# Revit family: equip-sink-elkay-lav-wall
name_source: partatom
category: Plumbing Fixtures
units: mm (PartAtom-declared; Revit-internal decimal feet)

## family parameters
Cut with Voids When Loaded = No
Host = Face
Part Type = Normal
Room Calculation Point = No
Round Connector Dimension = Use Radius
Shared = No

## types (10) — shared parameters
Assembly Code = D2010410
Bowl Drain Location FB = 0' - 3 1/2"
Bubbler CW Flow Rate = 2 GPM
Bubbler Material = Metal - Steel - Stainless - Chrome
Bubbler Nominal Dia = 0' - 0 1/2"
Bubbler Nominal Radius = 0' - 0 1/4"
CW Flow Rate = 2 GPM
Cost = -1 $
Default Elevation = 2' - 7 1/2"
Description = Wash-Up Lavatory Sinks
Drain Material = Metal - Steel - Stainless - Chrome
Faucet CL to Wall = 0' - 2 1/2"
Faucet Material = Metal - Steel - Stainless - Chrome
HW Flow Rate = 2 GPM
Keynote = D2010410
Manufacturer = Elkay Manufacturing
MasterFormat Number = 22.42.16.16
MasterFormat Title = Commercial Sinks
Nominal Dia = 0' - 0 1/2"
Nominal Radius = 0' - 0 1/4"
OmniClass Code = 23.45.05.14.14.27
OmniClass Title = Service Sinks
Reference Level to Back Plane = 0' - 0"
Sanitary Flow Rate = 10 GPM
Sanitary Nominal Dia = 0' - 1 1/2"
Sanitary Nominal Radius = 0' - 0 3/4"
Sink Ledge Back Width = 0' - 4 1/2"
Sink Ledge Back Width Hidden = 0' - 4 1/2"
Sink Material = Metal - Steel - Stainless - Chrome
Specification Sheet URL = http://www.elkayusa.com
Stem Material = Metal - Steel
URL = www.elkayusa.com
Vent Connection = Yes
zero-valued in all types: CWFU, HWFU, WFU

## per-type parameters (varying)
- ELVWO22193: Backsplash Height=0' - 2 3/4"; Bowl Depth=0' - 5 1/2"; Bowl Length=1' - 4"; Bowl Width=0' - 11 1/2"; Drain CL LR to Left Bowl Edge=0' - 8"; Faucet Hole Dia=0' - 1 1/2"; Faucet Hole One=Yes; Faucet Hole One Top=0' - 0 1/4"; Faucet Hole One to CL=0' - 4"; Faucet Hole Three=Yes; Faucet Hole Three Top=0' - 0 1/4"; Faucet Hole Two=Yes; Faucet Hole Two Top=0' - 0 1/4"; Hole One to Three=0' - 8"; Hole One to Two=0' - 4"; Hole Radius=0' - 0 3/4"; OverFlow=Yes; Overflow Void=0' - 0 3/16"; Sink Ledge Front Width=0' - 3"; Sink Ledge Front Width Hidden=0' - 3"; Sink Ledge Left Width=0' - 3"; Sink Ledge Left Width Hidden=0' - 3"; Sink Ledge Right Width=0' - 3"; Sink Ledge Right Width Hidden=0' - 3"; Sink Length=1' - 10"; Sink Width=1' - 7"
- ELVWO2219CS3: Backsplash Height=0' - 2 3/4"; Bowl Depth=0' - 5 1/2"; Bowl Length=1' - 4"; Bowl Width=0' - 11 1/2"; Drain CL LR to Left Bowl Edge=0' - 8"; Faucet Hole Dia=0' - 1 1/4"; Faucet Hole One=Yes; Faucet Hole One Top=0' - 0 1/4"; Faucet Hole One to CL=0' - 2"; Faucet Hole Three=Yes; Faucet Hole Three Top=0' - 0 1/4"; Faucet Hole Two=Yes; Faucet Hole Two Top=0' - 0 1/4"; Hole One to Three=0' - 4"; Hole One to Two=0' - 2"; Hole Radius=0' - 0 5/8"; OverFlow=Yes; Overflow Void=0' - 0 3/16"; Sink Ledge Front Width=0' - 3"; Sink Ledge Front Width Hidden=0' - 3"; Sink Ledge Left Width=0' - 3"; Sink Ledge Left Width Hidden=0' - 3"; Sink Ledge Right Width=0' - 3"; Sink Ledge Right Width Hidden=0' - 3"; Sink Length=1' - 10"; Sink Width=1' - 7"
- ELVWO22191: Backsplash Height=0' - 2 3/4"; Bowl Depth=0' - 5 1/2"; Bowl Length=1' - 4"; Bowl Width=0' - 11 1/2"; Drain CL LR to Left Bowl Edge=0' - 8"; Faucet Hole Dia=0' - 1 1/4"; Faucet Hole One=No; Faucet Hole One Top=0' - 0 1/8"; Faucet Hole One to CL=0' - 2"; Faucet Hole Three=No; Faucet Hole Three Top=0' - 0 1/8"; Faucet Hole Two=Yes; Faucet Hole Two Top=0' - 0 1/4"; Hole One to Three=0' - 4"; Hole One to Two=0' - 2"; Hole Radius=0' - 0 5/8"; OverFlow=Yes; Overflow Void=0' - 0 3/16"; Sink Ledge Front Width=0' - 3"; Sink Ledge Front Width Hidden=0' - 3"; Sink Ledge Left Width=0' - 3"; Sink Ledge Left Width Hidden=0' - 3"; Sink Ledge Right Width=0' - 3"; Sink Ledge Right Width Hidden=0' - 3"; Sink Length=1' - 10"; Sink Width=1' - 7"
- WCLWO1923OSD3: Backsplash Height=0' - 2 1/2"; Bowl Depth=0' - 4"; Bowl Length=1' - 1 1/2"; Bowl Width=1' - 4"; Drain CL LR to Left Bowl Edge=0' - 6 3/4"; Faucet Hole Dia=0' - 1 1/4"; Faucet Hole One=Yes; Faucet Hole One Top=0' - 0 1/4"; Faucet Hole One to CL=0' - 4"; Faucet Hole Three=Yes; Faucet Hole Three Top=0' - 0 1/4"; Faucet Hole Two=Yes; Faucet Hole Two Top=0' - 0 1/4"; Hole One to Three=0' - 8"; Hole One to Two=0' - 4"; Hole Radius=0' - 0 5/8"; OverFlow=Yes; Overflow Void=0' - 0 3/16"; Sink Ledge Front Width=0' - 2 1/2"; Sink Ledge Front Width Hidden=0' - 2 1/2"; Sink Ledge Left Width=0' - 2 3/4"; Sink Ledge Left Width Hidden=0' - 2 3/4"; Sink Ledge Right Width=0' - 2 3/4"; Sink Ledge Right Width Hidden=0' - 2 3/4"; Sink Length=1' - 7"; Sink Width=1' - 11"
- ELV22193: Backsplash Height=0' - 2 3/4"; Bowl Depth=0' - 5 1/2"; Bowl Length=1' - 4"; Bowl Width=0' - 11 1/2"; Drain CL LR to Left Bowl Edge=0' - 8"; Faucet Hole Dia=0' - 1 1/2"; Faucet Hole One=Yes; Faucet Hole One Top=0' - 0 1/4"; Faucet Hole One to CL=0' - 4"; Faucet Hole Three=Yes; Faucet Hole Three Top=0' - 0 1/4"; Faucet Hole Two=Yes; Faucet Hole Two Top=0' - 0 1/4"; Hole One to Three=0' - 8"; Hole One to Two=0' - 4"; Hole Radius=0' - 0 3/4"; OverFlow=No; Overflow Void=0' - 0 1/16"; Sink Ledge Front Width=0' - 3"; Sink Ledge Front Width Hidden=0' - 3"; Sink Ledge Left Width=0' - 3"; Sink Ledge Left Width Hidden=0' - 3"; Sink Ledge Right Width=0' - 3"; Sink Ledge Right Width Hidden=0' - 3"; Sink Length=1' - 10"; Sink Width=1' - 7"
- ELV22191: Backsplash Height=0' - 2 3/4"; Bowl Depth=0' - 5 1/2"; Bowl Length=1' - 4"; Bowl Width=0' - 11 1/2"; Drain CL LR to Left Bowl Edge=0' - 8"; Faucet Hole Dia=0' - 1 1/4"; Faucet Hole One=No; Faucet Hole One Top=0' - 0 1/8"; Faucet Hole One to CL=0' - 2"; Faucet Hole Three=No; Faucet Hole Three Top=0' - 0 1/8"; Faucet Hole Two=Yes; Faucet Hole Two Top=0' - 0 1/4"; Hole One to Three=0' - 4"; Hole One to Two=0' - 2"; Hole Radius=0' - 0 5/8"; OverFlow=No; Overflow Void=0' - 0 1/16"; Sink Ledge Front Width=0' - 3"; Sink Ledge Front Width Hidden=0' - 3"; Sink Ledge Left Width=0' - 3"; Sink Ledge Left Width Hidden=0' - 3"; Sink Ledge Right Width=0' - 3"; Sink Ledge Right Width Hidden=0' - 3"; Sink Length=1' - 10"; Sink Width=1' - 7"
- WCL1923OSD1: Backsplash Height=0' - 2 1/2"; Bowl Depth=0' - 4"; Bowl Length=1' - 2"; Bowl Width=1' - 4"; Drain CL LR to Left Bowl Edge=0' - 7"; Faucet Hole Dia=0' - 1 1/4"; Faucet Hole One=No; Faucet Hole One Top=0' - 0 1/8"; Faucet Hole One to CL=0' - 4"; Faucet Hole Three=No; Faucet Hole Three Top=0' - 0 1/8"; Faucet Hole Two=Yes; Faucet Hole Two Top=0' - 0 1/4"; Hole One to Three=0' - 8"; Hole One to Two=0' - 4"; Hole Radius=0' - 0 5/8"; OverFlow=No; Overflow Void=0' - 0 1/16"; Sink Ledge Front Width=0' - 2 1/2"; Sink Ledge Front Width Hidden=0' - 2 1/2"; Sink Ledge Left Width=0' - 2 1/2"; Sink Ledge Left Width Hidden=0' - 2 1/2"; Sink Ledge Right Width=0' - 2 1/2"; Sink Ledge Right Width Hidden=0' - 2 1/2"; Sink Length=1' - 7"; Sink Width=1' - 11"
- ELV2219CS3: Backsplash Height=0' - 2 3/4"; Bowl Depth=0' - 5 1/2"; Bowl Length=1' - 4"; Bowl Width=0' - 11 1/2"; Drain CL LR to Left Bowl Edge=0' - 8"; Faucet Hole Dia=0' - 1 1/4"; Faucet Hole One=Yes; Faucet Hole One Top=0' - 0 1/4"; Faucet Hole One to CL=0' - 2"; Faucet Hole Three=Yes; Faucet Hole Three Top=0' - 0 1/4"; Faucet Hole Two=Yes; Faucet Hole Two Top=0' - 0 1/4"; Hole One to Three=0' - 4"; Hole One to Two=0' - 2"; Hole Radius=0' - 0 5/8"; OverFlow=No; Overflow Void=0' - 0 1/16"; Sink Ledge Front Width=0' - 3"; Sink Ledge Front Width Hidden=0' - 3"; Sink Ledge Left Width=0' - 3"; Sink Ledge Left Width Hidden=0' - 3"; Sink Ledge Right Width=0' - 3"; Sink Ledge Right Width Hidden=0' - 3"; Sink Length=1' - 10"; Sink Width=1' - 7"
- WCL1923OSD3: Backsplash Height=0' - 2 1/2"; Bowl Depth=0' - 4"; Bowl Length=1' - 2"; Bowl Width=1' - 4"; Drain CL LR to Left Bowl Edge=0' - 7"; Faucet Hole Dia=0' - 1 1/2"; Faucet Hole One=Yes; Faucet Hole One Top=0' - 0 1/4"; Faucet Hole One to CL=0' - 4"; Faucet Hole Three=Yes; Faucet Hole Three Top=0' - 0 1/4"; Faucet Hole Two=Yes; Faucet Hole Two Top=0' - 0 1/4"; Hole One to Three=0' - 8"; Hole One to Two=0' - 4"; Hole Radius=0' - 0 3/4"; OverFlow=No; Overflow Void=0' - 0 1/16"; Sink Ledge Front Width=0' - 2 1/2"; Sink Ledge Front Width Hidden=0' - 2 1/2"; Sink Ledge Left Width=0' - 2 1/2"; Sink Ledge Left Width Hidden=0' - 2 1/2"; Sink Ledge Right Width=0' - 2 1/2"; Sink Ledge Right Width Hidden=0' - 2 1/2"; Sink Length=1' - 7"; Sink Width=1' - 11"
- WCL1923OSD0: Backsplash Height=0' - 2 1/2"; Bowl Depth=0' - 4"; Bowl Length=1' - 2"; Bowl Width=1' - 4"; Drain CL LR to Left Bowl Edge=0' - 7"; Faucet Hole Dia=0' - 1 1/4"; Faucet Hole One=No; Faucet Hole One Top=0' - 0 1/8"; Faucet Hole One to CL=0' - 5"; Faucet Hole Three=No; Faucet Hole Three Top=0' - 0 1/8"; Faucet Hole Two=No; Faucet Hole Two Top=0' - 0 1/8"; Hole One to Three=0' - 8"; Hole One to Two=0' - 4"; Hole Radius=0' - 0 5/8"; OverFlow=No; Overflow Void=0' - 0 1/16"; Sink Ledge Front Width=0' - 2 1/2"; Sink Ledge Front Width Hidden=0' - 2 1/2"; Sink Ledge Left Width=0' - 2 1/2"; Sink Ledge Left Width Hidden=0' - 2 1/2"; Sink Ledge Right Width=0' - 2 1/2"; Sink Ledge Right Width Hidden=0' - 2 1/2"; Sink Length=1' - 7"; Sink Width=1' - 11"

note: column(s) folded — value = type name in every type: Model, Sink Part

## geometry (parser evidence)
native form markers: Sweep x7
no freeform markers — native parametric forms only
